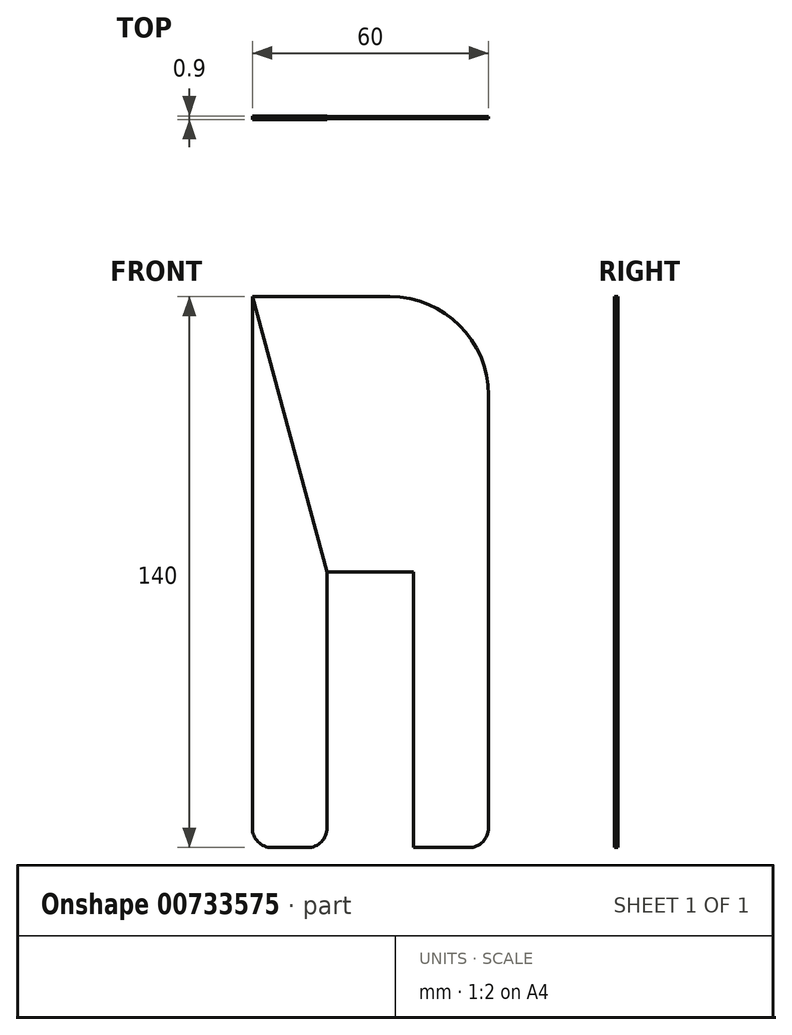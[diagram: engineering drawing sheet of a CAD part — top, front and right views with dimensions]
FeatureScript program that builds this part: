
annotation { "Feature Type Name" : "Feature", "Feature Type Description" : "" }
export const myFeature = defineFeature(function(context is Context, id is Id, definition is map)
    precondition{}
    {
        {
            var Q0;
            Q0=qCreatedBy(makeId("Front.planeOp"),FACE);
            var sketch = newSketch(context, id + "F0", { "sketchPlane" : qUnion([Q0])});
            skLineSegment(sketch, "E0.bottom", {"start": v(30, -70) * mm, "end": v(-30, -70) * mm});
            skLineSegment(sketch, "E0.top", {"start": v(30, 70) * mm, "end": v(-30, 70) * mm});
            skLineSegment(sketch, "E0.left", {"start": v(30, -70) * mm, "end": v(30, 70) * mm});
            skLineSegment(sketch, "E0.right", {"start": v(-30, -70) * mm, "end": v(-30, 70) * mm});
            skPoint(sketch, "E0.middle", {"position": v(0, 0) * mm});
            skSolve(sketch);
        }
        {
            var Q0;
            Q0 = qSketchRegion(id + "F0", true);
            extrude(context, id + "F1", {"entities" : qUnion([Q0]), "depth" : 0.5 * mm, "offsetDistance" : 25 * mm});
        }
        {
            var Q0;
            Q0=makeQuery(id+"F1.opExtrude","CAP_FACE",FACE,{"disambiguationData":[OSD([sQuery(id+"F0.wireOp",EDGE,"E0.bottom"),sQuery(id+"F0.wireOp",EDGE,"E0.top"),sQuery(id+"F0.wireOp",EDGE,"E0.left"),sQuery(id+"F0.wireOp",EDGE,"E0.right")])],"isStart":false});
            var sketch = newSketch(context, id + "F2", { "sketchPlane" : qUnion([Q0])});
            skLineSegment(sketch, "E1.bottom", {"start": v(-11, -70) * mm, "end": v(11, -70) * mm});
            skLineSegment(sketch, "E1.top", {"start": v(-11, 0) * mm, "end": v(11, 0) * mm});
            skLineSegment(sketch, "E1.left", {"start": v(-11, -70) * mm, "end": v(-11, 0) * mm});
            skLineSegment(sketch, "E1.right", {"start": v(11, -70) * mm, "end": v(11, 0) * mm});
            skSolve(sketch);
        }
        {
            var Q0;
            Q0 = qSketchRegion(id + "F2", true);
            extrude(context, id + "F3", {"entities" : qUnion([Q0]), "operationType" : NewBodyOperationType.REMOVE, "endBound" : BoundingType.UP_TO_NEXT, "oppositeDirection" : true, "depth" : 25 * mm, "offsetDistance" : 25 * mm});
        }
        {
            var Q0;
            Q0=makeQuery(id+"F1.opExtrude","CAP_FACE",FACE,{"disambiguationData":[OSD([sQuery(id+"F0.wireOp",EDGE,"E0.bottom"),sQuery(id+"F0.wireOp",EDGE,"E0.top"),sQuery(id+"F0.wireOp",EDGE,"E0.left"),sQuery(id+"F0.wireOp",EDGE,"E0.right")])],"isStart":false});
            var sketch = newSketch(context, id + "F4", { "sketchPlane" : qUnion([Q0])});
            skLineSegment(sketch, "E2.0", {"start": v(-30, -70) * mm, "end": v(-30, 70) * mm});
            skLineSegment(sketch, "E3.0", {"start": v(-11, -70) * mm, "end": v(-30, -70) * mm});
            skLineSegment(sketch, "E4.0", {"start": v(-11, -70) * mm, "end": v(-11, 0) * mm});
            skLineSegment(sketch, "E5", {"start": v(-11, 0) * mm, "end": v(-30, 70) * mm});
            skSolve(sketch);
        }
        {
            var Q0;
            Q0 = qSketchRegion(id + "F4", true);
            extrude(context, id + "F5", {"entities" : qUnion([Q0]), "operationType" : NewBodyOperationType.ADD, "depth" : 0.2 * mm, "offsetDistance" : 25 * mm});
        }
        {
            var Q0;
            Q0=makeQuery(id+"F1.opExtrude","CAP_FACE",FACE,{"disambiguationData":[OSD([sQuery(id+"F0.wireOp",EDGE,"E0.bottom"),sQuery(id+"F0.wireOp",EDGE,"E0.top"),sQuery(id+"F0.wireOp",EDGE,"E0.left"),sQuery(id+"F0.wireOp",EDGE,"E0.right")])],"isStart":true});
            var sketch = newSketch(context, id + "F6", { "sketchPlane" : qUnion([Q0])});
            skLineSegment(sketch, "E6.0.0", {"start": v(11, -70) * mm, "end": v(11, 0) * mm});
            skLineSegment(sketch, "E6.0.1", {"start": v(11, 0) * mm, "end": v(30, 70) * mm});
            skLineSegment(sketch, "E6.0.2", {"start": v(30, 70) * mm, "end": v(30, -70) * mm});
            skLineSegment(sketch, "E6.0.3", {"start": v(30, -70) * mm, "end": v(11, -70) * mm});
            skSolve(sketch);
        }
        {
            var Q0;
            Q0 = qSketchRegion(id + "F6", true);
            extrude(context, id + "F7", {"entities" : qUnion([Q0]), "operationType" : NewBodyOperationType.ADD, "depth" : 0.2 * mm, "offsetDistance" : 25 * mm});
        }
        {
            var Q0;
            Q0=makeQuery(id+"F1.opExtrude","SWEPT_EDGE",EDGE,{"disambiguationData":[OSD([sQuery(id+"F0.wireOp",EDGE,"E0.top"),sQuery(id+"F0.wireOp",EDGE,"E0.left")])]});
            fillet(context, id + "F8", {"entities" : qUnion([Q0]), "radius" : 25 * mm, "tangentPropagation" : true, "allowEdgeOverflow" : false});
        }
        {
            var Q0;
            Q0=makeQuery(id+"F7.boolean.opBoolean","MERGE",EDGE,{"derivedFrom":[makeQuery(id+"F5.boolean.opBoolean","MERGE",EDGE,{"derivedFrom":[makeQuery(id+"F1.opExtrude","SWEPT_EDGE",EDGE,{"disambiguationData":[OSD([sQuery(id+"F0.wireOp",EDGE,"E0.bottom"),sQuery(id+"F0.wireOp",EDGE,"E0.right")])]}),makeQuery(id+"F5.opExtrude","SWEPT_EDGE",EDGE,{"disambiguationData":[OSD([sQuery(id+"F4.wireOp",EDGE,"E2.0"),sQuery(id+"F4.wireOp",EDGE,"E3.0")])]})]}),makeQuery(id+"F7.opExtrude","SWEPT_EDGE",EDGE,{"disambiguationData":[OSD([sQuery(id+"F6.wireOp",EDGE,"E6.0.2"),sQuery(id+"F6.wireOp",EDGE,"E6.0.3")])]})]});
            var Q1;
            Q1=makeQuery(id+"F7.boolean.opBoolean","MERGE",EDGE,{"derivedFrom":[makeQuery(id+"F5.boolean.opBoolean","MERGE",EDGE,{"derivedFrom":[makeQuery(id+"F3.boolean.opBoolean","COPY",EDGE,{"derivedFrom":makeQuery(id+"F3.opExtrude","SWEPT_EDGE",EDGE,{"disambiguationData":[OSD([sQuery(id+"F0.wireOp",EDGE,"E0.bottom"),sQuery(id+"F2.wireOp",EDGE,"E1.bottom"),sQuery(id+"F2.wireOp",EDGE,"E1.left")])]})}),makeQuery(id+"F5.opExtrude","SWEPT_EDGE",EDGE,{"disambiguationData":[OSD([sQuery(id+"F4.wireOp",EDGE,"E3.0"),sQuery(id+"F4.wireOp",EDGE,"E4.0")])]})]}),makeQuery(id+"F7.opExtrude","SWEPT_EDGE",EDGE,{"disambiguationData":[OSD([sQuery(id+"F6.wireOp",EDGE,"E6.0.0"),sQuery(id+"F6.wireOp",EDGE,"E6.0.3")])]})]});
            var Q2;
            Q2=makeQuery(id+"F3.boolean.opBoolean","COPY",EDGE,{"derivedFrom":makeQuery(id+"F3.opExtrude","SWEPT_EDGE",EDGE,{"disambiguationData":[OSD([sQuery(id+"F0.wireOp",EDGE,"E0.bottom"),sQuery(id+"F2.wireOp",EDGE,"E1.bottom"),sQuery(id+"F2.wireOp",EDGE,"E1.right")])]})});
            var Q3;
            Q3=makeQuery(id+"F1.opExtrude","SWEPT_EDGE",EDGE,{"disambiguationData":[OSD([sQuery(id+"F0.wireOp",EDGE,"E0.bottom"),sQuery(id+"F0.wireOp",EDGE,"E0.left")])]});
            fillet(context, id + "F9", {"entities" : qUnion([Q0, Q1, Q2, Q3]), "radius" : 5 * mm, "tangentPropagation" : true, "allowEdgeOverflow" : false});
        }
    });
